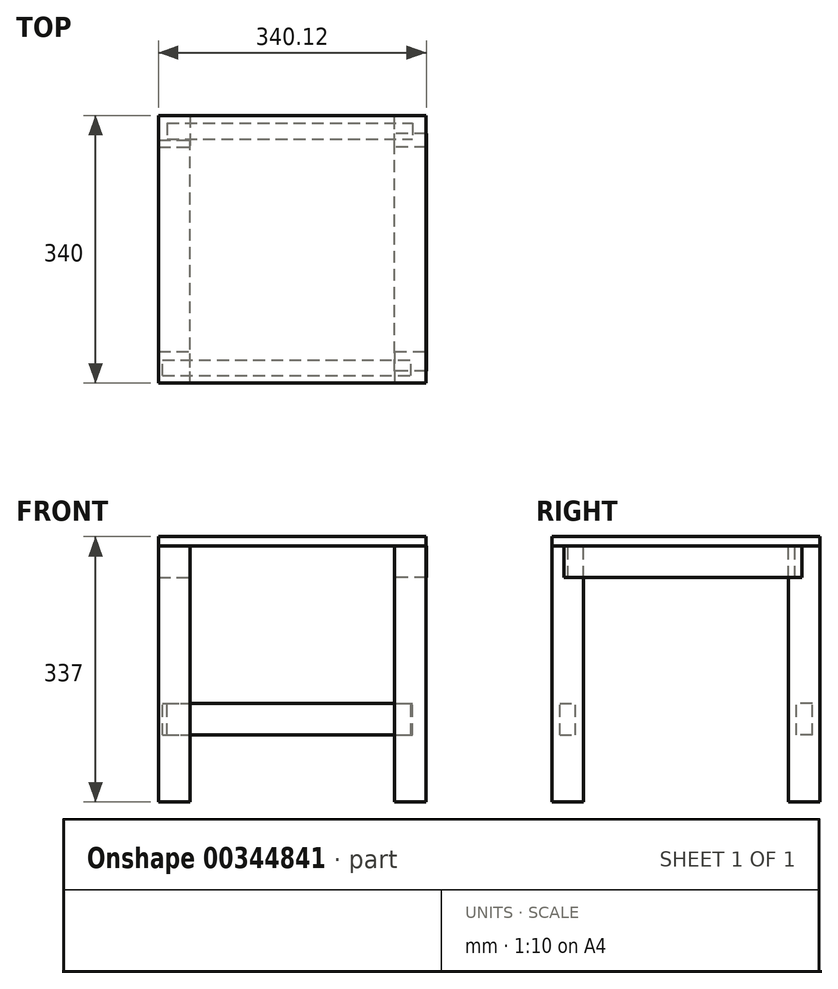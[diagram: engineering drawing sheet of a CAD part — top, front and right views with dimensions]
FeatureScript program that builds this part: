
annotation { "Feature Type Name" : "Feature", "Feature Type Description" : "" }
export const myFeature = defineFeature(function(context is Context, id is Id, definition is map)
    precondition{}
    {
        {
            var Q0;
            Q0=qCreatedBy(makeId("Top.planeOp"),FACE);
            var sketch = newSketch(context, id + "F0", { "sketchPlane" : qUnion([Q0])});
            skPoint(sketch, "E0.middle", {"position": v(0, 0) * mm});
            skLineSegment(sketch, "E1.bottom", {"start": v(170, 130) * mm, "end": v(130, 130) * mm});
            skLineSegment(sketch, "E1.top", {"start": v(170, 170) * mm, "end": v(130, 170) * mm});
            skLineSegment(sketch, "E1.left", {"start": v(170, 130) * mm, "end": v(170, 170) * mm});
            skLineSegment(sketch, "E1.right", {"start": v(130, 130) * mm, "end": v(130, 170) * mm});
            skPoint(sketch, "E1.middle", {"position": v(150, 150) * mm});
            skLineSegment(sketch, "E2.bottom", {"start": v(130, -130) * mm, "end": v(170, -130) * mm});
            skLineSegment(sketch, "E2.top", {"start": v(130, -170) * mm, "end": v(170, -170) * mm});
            skLineSegment(sketch, "E2.left", {"start": v(130, -130) * mm, "end": v(130, -170) * mm});
            skLineSegment(sketch, "E2.right", {"start": v(170, -130) * mm, "end": v(170, -170) * mm});
            skPoint(sketch, "E2.middle", {"position": v(150, -150) * mm});
            skLineSegment(sketch, "E3.bottom", {"start": v(-170, -170) * mm, "end": v(-130, -170) * mm});
            skLineSegment(sketch, "E3.top", {"start": v(-170, -130) * mm, "end": v(-130, -130) * mm});
            skLineSegment(sketch, "E3.left", {"start": v(-170, -170) * mm, "end": v(-170, -130) * mm});
            skLineSegment(sketch, "E3.right", {"start": v(-130, -170) * mm, "end": v(-130, -130) * mm});
            skPoint(sketch, "E3.middle", {"position": v(-150, -150) * mm});
            skLineSegment(sketch, "E4.bottom", {"start": v(-170, 170) * mm, "end": v(-130, 170) * mm});
            skLineSegment(sketch, "E4.top", {"start": v(-170, 130) * mm, "end": v(-130, 130) * mm});
            skLineSegment(sketch, "E4.left", {"start": v(-170, 170) * mm, "end": v(-170, 130) * mm});
            skLineSegment(sketch, "E4.right", {"start": v(-130, 170) * mm, "end": v(-130, 130) * mm});
            skPoint(sketch, "E4.middle", {"position": v(-150, 150) * mm});
            skSolve(sketch);
        }
        {
            var Q0;
            Q0=makeQuery(id+"F0.imprint","IMPRINT",FACE,{"disambiguationData":[TD([[makeQuery(id+"F0.imprint","IMPRINT",EDGE,{"derivedFrom":sQuery(id+"F0.wireOp",EDGE,"E3.bottom")}),1.0]])]});
            var Q1;
            Q1=makeQuery(id+"F0.imprint","IMPRINT",FACE,{"disambiguationData":[TD([[makeQuery(id+"F0.imprint","IMPRINT",EDGE,{"derivedFrom":sQuery(id+"F0.wireOp",EDGE,"E4.bottom")}),-1.0]])]});
            var Q2;
            Q2=makeQuery(id+"F0.imprint","IMPRINT",FACE,{"disambiguationData":[TD([[makeQuery(id+"F0.imprint","IMPRINT",EDGE,{"derivedFrom":sQuery(id+"F0.wireOp",EDGE,"E2.bottom")}),-1.0]])]});
            var Q3;
            Q3=makeQuery(id+"F0.imprint","IMPRINT",FACE,{"disambiguationData":[TD([[makeQuery(id+"F0.imprint","IMPRINT",EDGE,{"derivedFrom":sQuery(id+"F0.wireOp",EDGE,"E1.bottom")}),-1.0]])]});
            extrude(context, id + "F1", {"entities" : qUnion([Q0, Q1, Q2, Q3]), "oppositeDirection" : true, "depth" : 325 * mm});
        }
        {
            var Q0;
            Q0=makeQuery(id+"F1.opExtrude","CAP_FACE",FACE,{"disambiguationData":[OSD([sQuery(id+"F0.wireOp",EDGE,"E3.bottom"),sQuery(id+"F0.wireOp",EDGE,"E3.top"),sQuery(id+"F0.wireOp",EDGE,"E3.left"),sQuery(id+"F0.wireOp",EDGE,"E3.right")])],"isStart":true});
            var sketch = newSketch(context, id + "F2", { "sketchPlane" : qUnion([Q0])});
            skLineSegment(sketch, "E5.bottom", {"start": v(-170, -150) * mm, "end": v(-129.68, -150) * mm});
            skLineSegment(sketch, "E5.top", {"start": v(-170, 138.56) * mm, "end": v(-129.68, 138.56) * mm});
            skLineSegment(sketch, "E5.left", {"start": v(-170, -150) * mm, "end": v(-170, 138.56) * mm});
            skLineSegment(sketch, "E5.right", {"start": v(-129.68, -150) * mm, "end": v(-129.68, 138.56) * mm});
            skLineSegment(sketch, "E6.bottom", {"start": v(170.12, -154.83) * mm, "end": v(129.68, -154.83) * mm});
            skLineSegment(sketch, "E6.top", {"start": v(170.12, 146.94) * mm, "end": v(129.68, 146.94) * mm});
            skLineSegment(sketch, "E6.left", {"start": v(170.12, -154.83) * mm, "end": v(170.12, 146.94) * mm});
            skLineSegment(sketch, "E6.right", {"start": v(129.68, -154.83) * mm, "end": v(129.68, 146.94) * mm});
            skSolve(sketch);
        }
        {
            var Q0;
            {var subQ3=sQuery(id+"F2.wireOp",EDGE,"E5.top");Q0=makeQuery(id+"F2.imprint","IMPRINT",FACE,{"disambiguationData":[TD([[makeQuery(id+"F2.imprint","IMPRINT",EDGE,{"derivedFrom":subQ3}),-1.0]])]});}
            var Q1;
            Q1=makeQuery(id+"F2.imprint","IMPRINT",FACE,{"disambiguationData":[TD([[makeQuery(id+"F2.imprint","IMPRINT",EDGE,{"derivedFrom":sQuery(id+"F2.wireOp",EDGE,"E6.bottom")}),-1.0]])]});
            extrude(context, id + "F3", {"entities" : qUnion([Q0, Q1]), "oppositeDirection" : true, "depth" : 40 * mm});
        }
        {
            var Q0;
            Q0=qCreatedBy(makeId("Top.planeOp"),FACE);
            cPlane(context, id + "F4", {"entities" : qUnion([Q0]), "cplaneType" : CPlaneType.OFFSET, "offset" : 200 * mm, "oppositeDirection" : true, "width" : 150 * mm, "height" : 150 * mm});
        }
        {
            var Q0;
            Q0=qCreatedBy(id+"F4.planeOp",FACE);
            var sketch = newSketch(context, id + "F5", { "sketchPlane" : qUnion([Q0])});
            skLineSegment(sketch, "E7.top", {"start": v(-164.7, -160.43) * mm, "end": v(-112.8, -160.43) * mm});
            skLineSegment(sketch, "E7.left", {"start": v(-164.7, -170.43) * mm, "end": v(-164.7, -160.43) * mm});
            skLineSegment(sketch, "E8.bottom", {"start": v(-164.7, -160.43) * mm, "end": v(150.45, -160.43) * mm});
            skLineSegment(sketch, "E8.top", {"start": v(-164.7, -140.43) * mm, "end": v(150.45, -140.43) * mm});
            skLineSegment(sketch, "E8.left", {"start": v(-164.7, -160.43) * mm, "end": v(-164.7, -140.43) * mm});
            skLineSegment(sketch, "E8.right", {"start": v(150.45, -160.43) * mm, "end": v(150.45, -140.43) * mm});
            skLineSegment(sketch, "E9.bottom", {"start": v(-166.11, 170.26) * mm, "end": v(-152.3, 170.26) * mm});
            skLineSegment(sketch, "E9.top", {"start": v(-166.11, 160.26) * mm, "end": v(-152.3, 160.26) * mm});
            skLineSegment(sketch, "E9.left", {"start": v(-166.11, 170.26) * mm, "end": v(-166.11, 160.26) * mm});
            skLineSegment(sketch, "E9.right", {"start": v(-152.3, 170.26) * mm, "end": v(-152.3, 160.26) * mm});
            skLineSegment(sketch, "E10.bottom", {"start": v(-159.21, 160.26) * mm, "end": v(152.42, 160.26) * mm});
            skLineSegment(sketch, "E10.top", {"start": v(-159.21, 140.26) * mm, "end": v(152.42, 140.26) * mm});
            skLineSegment(sketch, "E10.left", {"start": v(-159.21, 160.26) * mm, "end": v(-159.21, 140.26) * mm});
            skLineSegment(sketch, "E10.right", {"start": v(152.42, 160.26) * mm, "end": v(152.42, 140.26) * mm});
            skSolve(sketch);
        }
        {
            var Q0;
            Q0=makeQuery(id+"F5.imprint","IMPRINT",FACE,{"disambiguationData":[TD([[makeQuery(id+"F5.imprint","IMPRINT",EDGE,{"derivedFrom":sQuery(id+"F5.wireOp",EDGE,"E8.top")}),-1.0]])]});
            var Q1;
            Q1=makeQuery(id+"F5.imprint","IMPRINT",FACE,{"disambiguationData":[TD([[makeQuery(id+"F5.imprint","IMPRINT",EDGE,{"derivedFrom":sQuery(id+"F5.wireOp",EDGE,"E10.top")}),1.0]])]});
            extrude(context, id + "F6", {"entities" : qUnion([Q0, Q1]), "oppositeDirection" : true, "depth" : 40 * mm});
        }
        {
            var Q0;
            Q0=qCreatedBy(makeId("Top.planeOp"),FACE);
            var sketch = newSketch(context, id + "F7", { "sketchPlane" : qUnion([Q0])});
            skLineSegment(sketch, "E11.bottom", {"start": v(-170, 170) * mm, "end": v(170, 170) * mm});
            skLineSegment(sketch, "E11.top", {"start": v(-170, -170) * mm, "end": v(170, -170) * mm});
            skLineSegment(sketch, "E11.left", {"start": v(-170, 170) * mm, "end": v(-170, -170) * mm});
            skLineSegment(sketch, "E11.right", {"start": v(170, 170) * mm, "end": v(170, -170) * mm});
            skPoint(sketch, "E11.middle", {"position": v(0, 0) * mm});
            skSolve(sketch);
        }
        {
            var Q0;
            Q0=makeQuery(id+"F7.imprint","IMPRINT",FACE,{"disambiguationData":[TD([[makeQuery(id+"F7.imprint","IMPRINT",EDGE,{"derivedFrom":sQuery(id+"F7.wireOp",EDGE,"E11.bottom")}),-1.0]])]});
            extrude(context, id + "F8", {"entities" : qUnion([Q0]), "depth" : 12 * mm});
        }
    });
